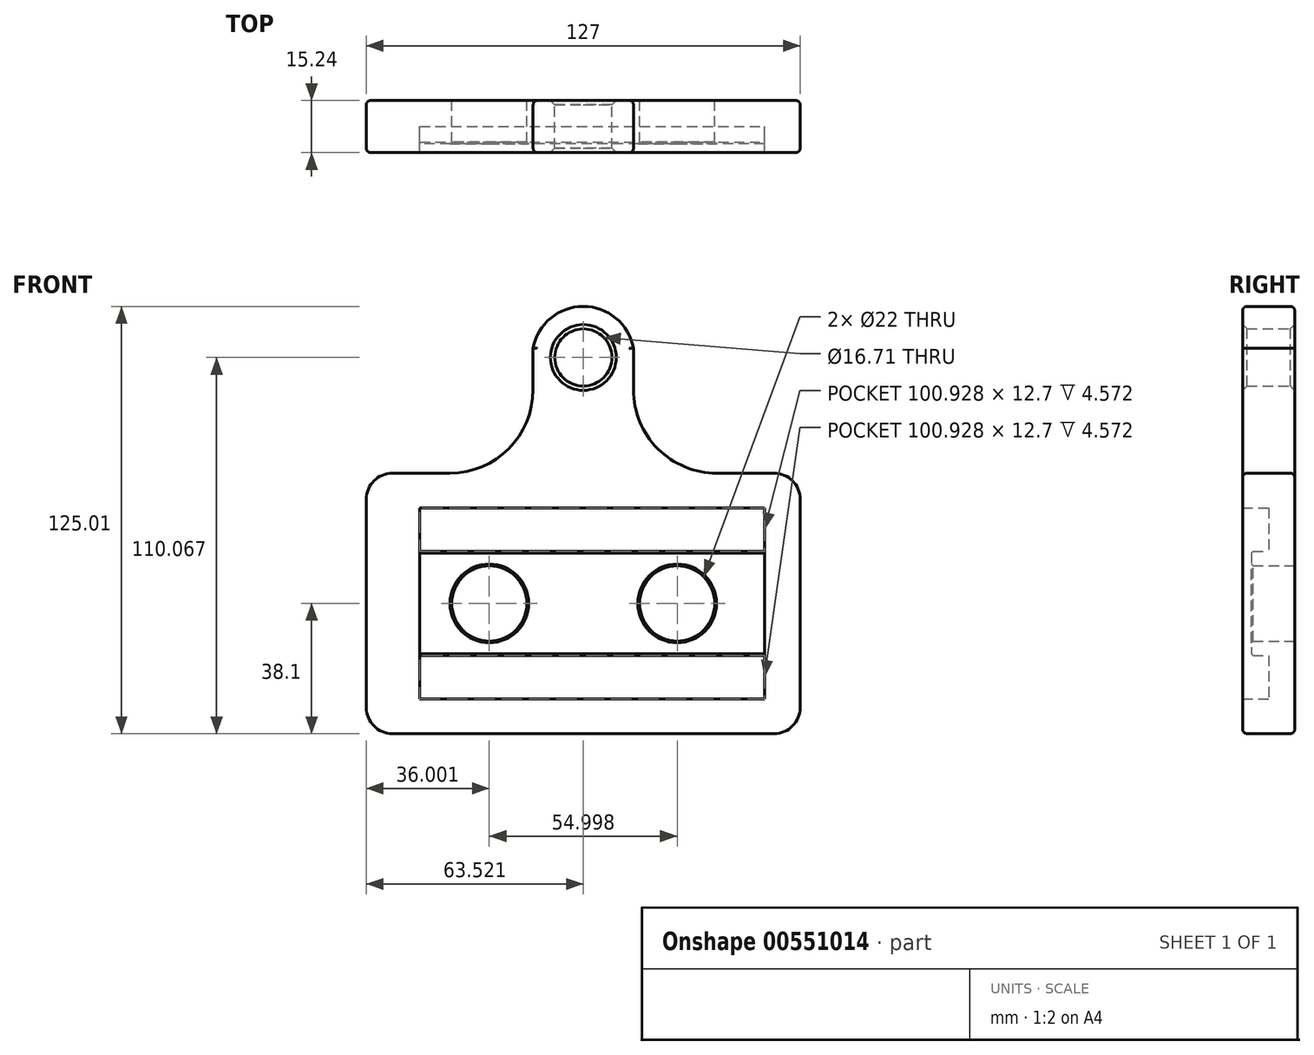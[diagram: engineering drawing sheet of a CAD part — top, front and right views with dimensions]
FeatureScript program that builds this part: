
annotation { "Feature Type Name" : "Feature", "Feature Type Description" : "" }
export const myFeature = defineFeature(function(context is Context, id is Id, definition is map)
    precondition{}
    {
        {
            var Q0;
            Q0=qCreatedBy(makeId("Front.planeOp"),FACE);
            var sketch = newSketch(context, id + "F0", { "sketchPlane" : qUnion([Q0])});
            skLineSegment(sketch, "E0.bottom", {"start": v(-63.5, -38.1) * mm, "end": v(63.5, -38.1) * mm});
            skLineSegment(sketch, "E0.top", {"start": v(-63.5, 38.1) * mm, "end": v(-39.1, 38.1) * mm});
            skLineSegment(sketch, "E0.left", {"start": v(-63.5, -38.1) * mm, "end": v(-63.5, 38.1) * mm});
            skLineSegment(sketch, "E0.right", {"start": v(63.5, -38.1) * mm, "end": v(63.5, 38.1) * mm});
            skPoint(sketch, "E0.middle", {"position": v(0, 0) * mm});
            skPoint(sketch, "E1", {"position": v(0, 38.1) * mm});
            skLineSegment(sketch, "E2.bottom", {"start": v(0, 86.91) * mm, "end": v(0.04, 86.91) * mm});
            skLineSegment(sketch, "E2.left", {"start": v(-14.67, 74.7) * mm, "end": v(-14.68, 62.5) * mm});
            skLineSegment(sketch, "E2.right", {"start": v(14.71, 74.7) * mm, "end": v(14.7, 62.5) * mm});
            skPoint(sketch, "E3", {"position": v(-14.69, 38.1) * mm});
            skPoint(sketch, "E4", {"position": v(14.69, 38.1) * mm});
            skPoint(sketch, "E2.top.end.orphan", {"position": v(14.66, -10.71) * mm});
            skPoint(sketch, "E2.top.start.orphan", {"position": v(-14.72, -10.71) * mm});
            skLineSegment(sketch, "E5.trimOffspring", {"start": v(39.1, 38.1) * mm, "end": v(63.5, 38.1) * mm});
            skPoint(sketch, "E6", {"position": v(-39.1, 38.1) * mm});
            skPoint(sketch, "E7", {"position": v(39.1, 38.1) * mm});
            skPoint(sketch, "E8", {"position": v(14.7, 62.5) * mm});
            skPoint(sketch, "E9", {"position": v(-14.68, 62.5) * mm});
            skArc(sketch, "E10", {"start": v(-39.1, 38.1) * mm, "mid": v(-21.83, 45.25) * mm, "end": v(-14.68, 62.5) * mm});
            skArc(sketch, "E11", {"start": v(14.7, 62.5) * mm, "mid": v(21.84, 45.25) * mm, "end": v(39.1, 38.1) * mm});
            skPoint(sketch, "E12", {"position": v(0, 86.91) * mm});
            skArc(sketch, "E13", {"start": v(14.71, 74.7) * mm, "mid": v(0.02, 86.91) * mm, "end": v(-14.67, 74.7) * mm});
            skPoint(sketch, "E14.orphan", {"position": v(-14.66, 86.91) * mm});
            skPoint(sketch, "E15.orphan", {"position": v(14.72, 86.91) * mm});
            skCircle(sketch, "E16", {"center": v(0.02, 71.97) * mm, "radius": 8.36 * mm});
            skPoint(sketch, "E17", {"position": v(-118.94, 62.01) * mm});
            skCircle(sketch, "E18", {"center": v(-27.5, 0) * mm, "radius": 11 * mm});
            skCircle(sketch, "E19.MirrorC", {"center": v(27.5, 0) * mm, "radius": 11 * mm});
            skLineSegment(sketch, "E20.bottom", {"start": v(-47.85, 27.94) * mm, "end": v(53.08, 27.94) * mm});
            skLineSegment(sketch, "E20.top", {"start": v(-47.85, -27.94) * mm, "end": v(53.08, -27.94) * mm});
            skLineSegment(sketch, "E20.left", {"start": v(-47.85, 27.94) * mm, "end": v(-47.85, -27.94) * mm});
            skLineSegment(sketch, "E20.right", {"start": v(53.08, 27.94) * mm, "end": v(53.08, -27.94) * mm});
            skPoint(sketch, "E20.middle", {"position": v(2.62, 0) * mm});
            skLineSegment(sketch, "E21", {"start": v(-47.85, 15.24) * mm, "end": v(53.08, 15.24) * mm});
            skLineSegment(sketch, "E22", {"start": v(-47.85, -15.24) * mm, "end": v(53.08, -15.24) * mm});
            skLineSegment(sketch, "E23", {"start": v(-47.85, 0) * mm, "end": v(-38.5, 0) * mm});
            skLineSegment(sketch, "E24.trimOffspring", {"start": v(38.5, 0) * mm, "end": v(53.08, 0) * mm});
            skLineSegment(sketch, "E25", {"start": v(-16.5, 0) * mm, "end": v(16.5, 0) * mm});
            skSolve(sketch);
        }
        {
            var Q0;
            Q0 = qSketchRegion(id + "F0", true);
            var Q1;
            Q1=makeQuery(id+"F0.imprint","IMPRINT",FACE,{"disambiguationData":[TD([[makeQuery(id+"F0.imprint","IMPRINT",EDGE,{"derivedFrom":sQuery(id+"F0.wireOp",EDGE,"E0.bottom")}),1.0]])]});
            extrude(context, id + "F1", {"entities" : qUnion([Q0, Q1]), "depth" : 15.24 * mm, "offsetDistance" : 25.4 * mm});
        }
        {
            var Q0;
            Q0=makeQuery(id+"F1.opExtrude","SWEPT_EDGE",EDGE,{"disambiguationData":[OSD([sQuery(id+"F0.wireOp",EDGE,"E0.right"),sQuery(id+"F0.wireOp",EDGE,"E5.trimOffspring")])]});
            var Q1;
            Q1=makeQuery(id+"F1.opExtrude","SWEPT_EDGE",EDGE,{"disambiguationData":[OSD([sQuery(id+"F0.wireOp",EDGE,"E0.top"),sQuery(id+"F0.wireOp",EDGE,"E0.left")])]});
            var Q2;
            Q2=makeQuery(id+"F1.opExtrude","SWEPT_EDGE",EDGE,{"disambiguationData":[OSD([sQuery(id+"F0.wireOp",EDGE,"E0.bottom"),sQuery(id+"F0.wireOp",EDGE,"E0.right")])]});
            var Q3;
            Q3=makeQuery(id+"F1.opExtrude","SWEPT_EDGE",EDGE,{"disambiguationData":[OSD([sQuery(id+"F0.wireOp",EDGE,"E0.bottom"),sQuery(id+"F0.wireOp",EDGE,"E0.left")])]});
            fillet(context, id + "F2", {"entities" : qUnion([Q0, Q1, Q2, Q3]), "radius" : 7.62 * mm, "tangentPropagation" : true, "allowEdgeOverflow" : false});
        }
        {
            var Q0;
            Q0=makeQuery(id+"F1.opExtrude","CAP_EDGE",EDGE,{"disambiguationData":[OSD([sQuery(id+"F0.wireOp",EDGE,"E5.trimOffspring")])],"isStart":true});
            var Q1;
            Q1=makeQuery(id+"F1.opExtrude","CAP_EDGE",EDGE,{"disambiguationData":[OSD([sQuery(id+"F0.wireOp",EDGE,"E11")])],"isStart":true});
            var Q2;
            Q2=makeQuery(id+"F1.opExtrude","CAP_EDGE",EDGE,{"disambiguationData":[OSD([sQuery(id+"F0.wireOp",EDGE,"E10")])],"isStart":false});
            var Q3;
            Q3=makeQuery(id+"F1.opExtrude","CAP_EDGE",EDGE,{"disambiguationData":[OSD([sQuery(id+"F0.wireOp",EDGE,"E13")])],"isStart":false});
            var Q4;
            Q4=makeQuery(id+"F1.opExtrude","CAP_EDGE",EDGE,{"disambiguationData":[OSD([sQuery(id+"F0.wireOp",EDGE,"E13")])],"isStart":true});
            fillet(context, id + "F3", {"entities" : qUnion([Q0, Q1, Q2, Q3, Q4]), "radius" : 1.27 * mm, "tangentPropagation" : true, "allowEdgeOverflow" : false});
        }
        {
            var Q0;
            Q0=makeQuery(id+"F1.opExtrude","CAP_EDGE",EDGE,{"disambiguationData":[OSD([sQuery(id+"F0.wireOp",EDGE,"E16")])],"isStart":false});
            var Q1;
            Q1=makeQuery(id+"F1.opExtrude","CAP_EDGE",EDGE,{"disambiguationData":[OSD([sQuery(id+"F0.wireOp",EDGE,"E16")])],"isStart":true});
            var Q2;
            Q2=makeQuery(id+"F1.opExtrude","CAP_EDGE",EDGE,{"disambiguationData":[OSD([sQuery(id+"F0.wireOp",EDGE,"E19.MirrorC")])],"isStart":true});
            var Q3;
            Q3=makeQuery(id+"F1.opExtrude","CAP_EDGE",EDGE,{"disambiguationData":[OSD([sQuery(id+"F0.wireOp",EDGE,"E19.MirrorC")])],"isStart":false});
            var Q4;
            Q4=makeQuery(id+"F1.opExtrude","CAP_EDGE",EDGE,{"disambiguationData":[OSD([sQuery(id+"F0.wireOp",EDGE,"E18")])],"isStart":true});
            var Q5;
            Q5=makeQuery(id+"F1.opExtrude","CAP_EDGE",EDGE,{"disambiguationData":[OSD([sQuery(id+"F0.wireOp",EDGE,"E18")])],"isStart":false});
            chamfer(context, id + "F4", {"entities" : qUnion([Q0, Q1, Q2, Q3, Q4, Q5]), "width" : 1.27 * mm, "tangentPropagation" : true});
        }
        {
            var Q0;
            Q0=makeQuery(id+"F0.imprint","IMPRINT",FACE,{"disambiguationData":[TD([[makeQuery(id+"F0.imprint","IMPRINT",EDGE,{"derivedFrom":sQuery(id+"F0.wireOp",EDGE,"E18")}),-1.0]])]});
            extrude(context, id + "F5", {"entities" : qUnion([Q0]), "operationType" : NewBodyOperationType.ADD, "depth" : 12.7 * mm, "offsetDistance" : 25.4 * mm});
        }
        {
            var Q0;
            {var subQ0=sQuery(id+"F0.wireOp",EDGE,"E20.bottom");Q0=makeQuery(id+"F0.imprint","IMPRINT",FACE,{"disambiguationData":[TD([[makeQuery(id+"F0.imprint","IMPRINT",EDGE,{"derivedFrom":subQ0}),-1.0]])]});}
            var Q1;
            {var subQ0=sQuery(id+"F0.wireOp",EDGE,"E20.top");Q1=makeQuery(id+"F0.imprint","IMPRINT",FACE,{"disambiguationData":[TD([[makeQuery(id+"F0.imprint","IMPRINT",EDGE,{"derivedFrom":subQ0}),1.0]])]});}
            extrude(context, id + "F6", {"entities" : qUnion([Q0, Q1]), "operationType" : NewBodyOperationType.ADD, "depth" : 7.62 * mm, "offsetDistance" : 25.4 * mm});
        }
        {
            var Q0;
            Q0=makeQuery(id+"F5.opExtrude","CAP_EDGE",EDGE,{"disambiguationData":[OSD([sQuery(id+"F0.wireOp",EDGE,"E22")])],"isStart":false});
            var Q1;
            Q1=makeQuery(id+"F5.opExtrude","CAP_EDGE",EDGE,{"disambiguationData":[OSD([sQuery(id+"F0.wireOp",EDGE,"E21")])],"isStart":false});
            var Q2;
            Q2=makeQuery(id+"F5.opExtrude","CAP_EDGE",EDGE,{"disambiguationData":[OSD([sQuery(id+"F0.wireOp",EDGE,"E18")])],"isStart":false});
            var Q3;
            Q3=makeQuery(id+"F5.opExtrude","CAP_EDGE",EDGE,{"disambiguationData":[OSD([sQuery(id+"F0.wireOp",EDGE,"E19.MirrorC")])],"isStart":false});
            chamfer(context, id + "F7", {"entities" : qUnion([Q0, Q1, Q2, Q3]), "width" : 0.5 * mm, "tangentPropagation" : true});
        }
    });
